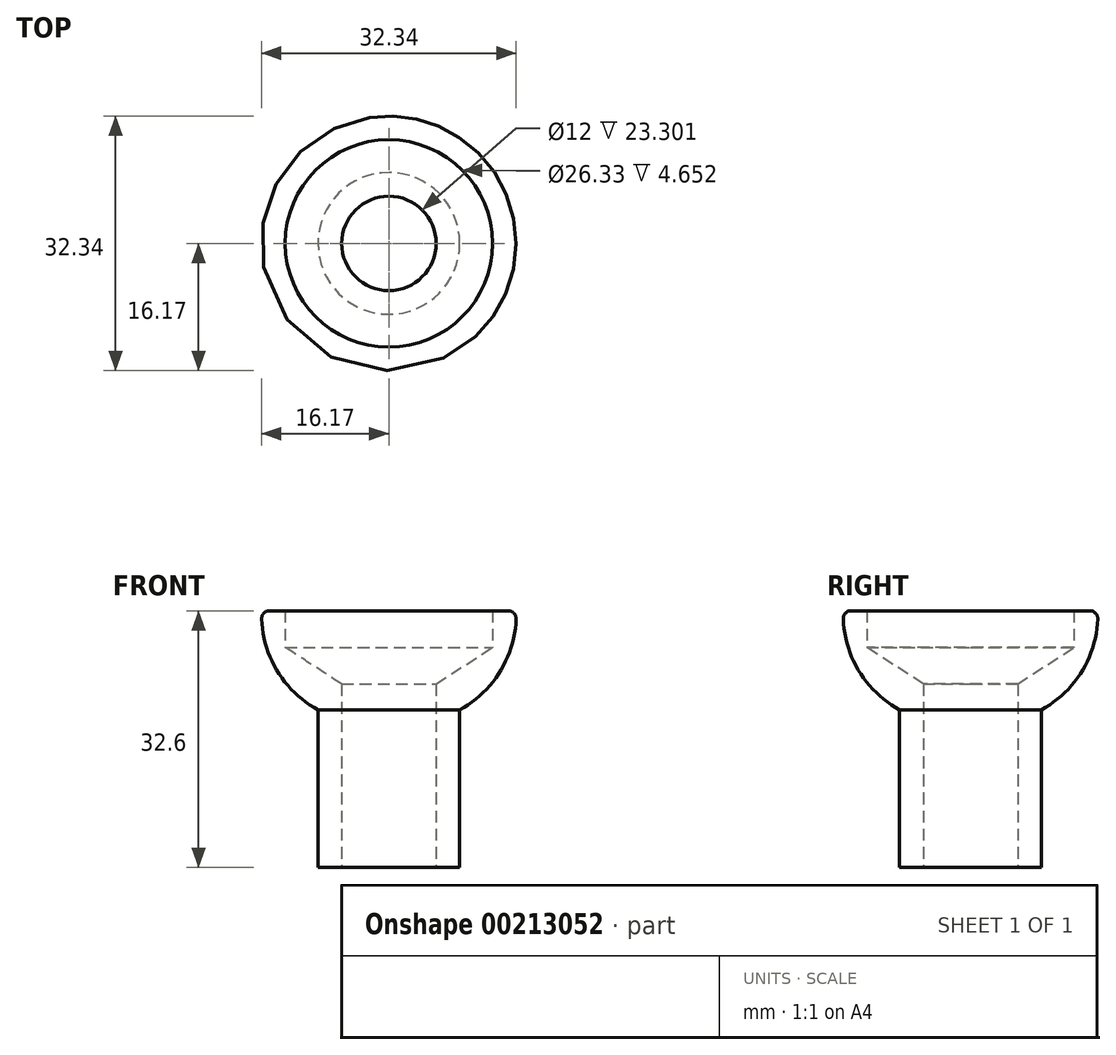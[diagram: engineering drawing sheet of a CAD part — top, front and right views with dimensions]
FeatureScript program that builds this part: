
annotation { "Feature Type Name" : "Feature", "Feature Type Description" : "" }
export const myFeature = defineFeature(function(context is Context, id is Id, definition is map)
    precondition{}
    {
        {
            var Q0;
            Q0=qCreatedBy(makeId("Right.planeOp"),FACE);
            var sketch = newSketch(context, id + "F0", { "sketchPlane" : qUnion([Q0])});
            skLineSegment(sketch, "E0", {"start": v(0, 0) * mm, "end": v(0, 11.48) * mm});
            skLineSegment(sketch, "E1", {"start": v(6, 0) * mm, "end": v(9, 0) * mm});
            skLineSegment(sketch, "E2", {"start": v(9, 0) * mm, "end": v(9, 20) * mm});
            skLineSegment(sketch, "E3", {"start": v(6, 0) * mm, "end": v(6, 20) * mm});
            skArc(sketch, "E4", {"start": v(9, 20) * mm, "mid": v(14.37, 25.29) * mm, "end": v(16.17, 32.6) * mm});
            skLineSegment(sketch, "E5", {"start": v(16.17, 32.6) * mm, "end": v(13.17, 32.6) * mm});
            skLineSegment(sketch, "E6", {"start": v(13.17, 32.6) * mm, "end": v(13.17, 27.95) * mm});
            skLineSegment(sketch, "E7", {"start": v(6, 20) * mm, "end": v(6, 23.3) * mm});
            skLineSegment(sketch, "E8", {"start": v(13.17, 27.95) * mm, "end": v(6, 23.3) * mm});
            skSolve(sketch);
        }
        {
            var Q0;
            Q0=makeQuery(id+"F0.imprint","IMPRINT",FACE,{"disambiguationData":[TD([[makeQuery(id+"F0.imprint","IMPRINT",EDGE,{"derivedFrom":sQuery(id+"F0.wireOp",EDGE,"E1")}),1.0]])]});
            var Q1;
            Q1=sQuery(id+"F0.wireOp",EDGE,"E0");
            revolve(context, id + "F1", {"entities" : qUnion([Q0]), "axis" : qUnion([Q1]), "revolveType" : RevolveType.FULL});
        }
        {
            var Q0;
            Q0=makeQuery(id+"F1.opRevolve","SWEPT_EDGE",EDGE,{"disambiguationData":[OSD([sQuery(id+"F0.wireOp",EDGE,"E4"),sQuery(id+"F0.wireOp",EDGE,"E5")])]});
            fillet(context, id + "F2", {"entities" : qUnion([Q0]), "radius" : 1 * mm, "tangentPropagation" : true, "allowEdgeOverflow" : false});
        }
    });
